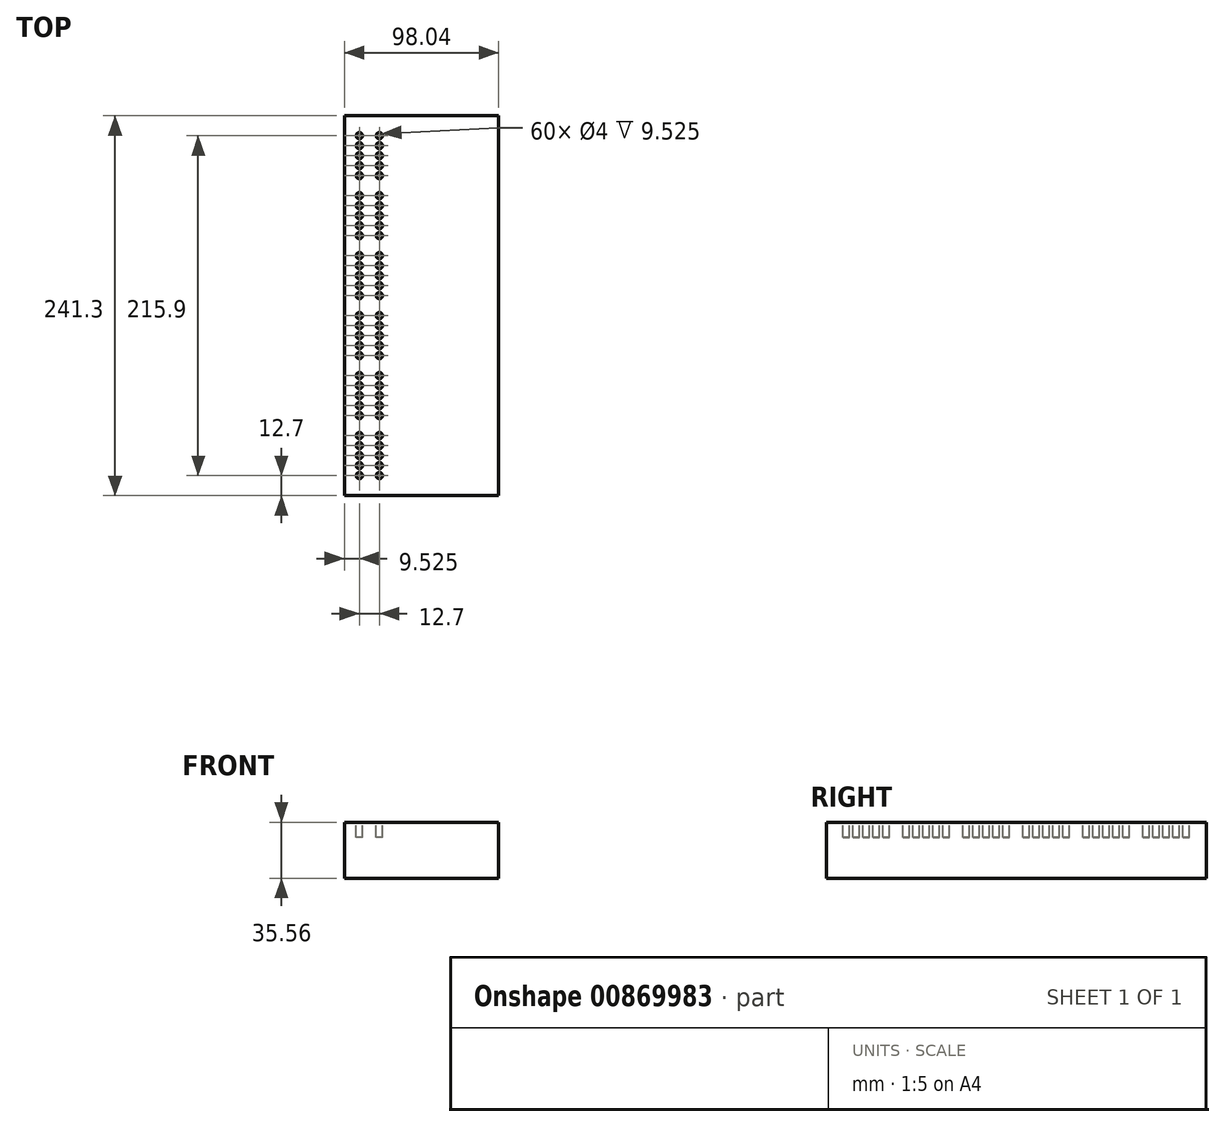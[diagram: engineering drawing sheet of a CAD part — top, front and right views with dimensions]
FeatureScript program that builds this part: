
annotation { "Feature Type Name" : "Feature", "Feature Type Description" : "" }
export const myFeature = defineFeature(function(context is Context, id is Id, definition is map)
    precondition{}
    {
        {
            var Q0;
            Q0=qCreatedBy(makeId("Top.planeOp"),FACE);
            var sketch = newSketch(context, id + "F0", { "sketchPlane" : qUnion([Q0])});
            skLineSegment(sketch, "E0.bottom", {"start": v(0, 241.3) * mm, "end": v(98.04, 241.3) * mm});
            skLineSegment(sketch, "E0.top", {"start": v(0, 0) * mm, "end": v(98.04, 0) * mm});
            skLineSegment(sketch, "E0.left", {"start": v(0, 241.3) * mm, "end": v(0, 0) * mm});
            skLineSegment(sketch, "E0.right", {"start": v(98.04, 241.3) * mm, "end": v(98.04, 0) * mm});
            skSolve(sketch);
        }
        {
            var Q0;
            Q0=makeQuery(id+"F0.imprint","IMPRINT",FACE,{"disambiguationData":[TD([[makeQuery(id+"F0.imprint","IMPRINT",EDGE,{"derivedFrom":sQuery(id+"F0.wireOp",EDGE,"E0.bottom")}),-1.0]])]});
            extrude(context, id + "F1", {"entities" : qUnion([Q0]), "depth" : 35.56 * mm, "offsetDistance" : 25.4 * mm});
        }
        {
            var Q0;
            Q0=makeQuery(id+"F1.opExtrude","CAP_FACE",FACE,{"disambiguationData":[OSD([sQuery(id+"F0.wireOp",EDGE,"E0.bottom"),sQuery(id+"F0.wireOp",EDGE,"E0.top"),sQuery(id+"F0.wireOp",EDGE,"E0.left"),sQuery(id+"F0.wireOp",EDGE,"E0.right")])],"isStart":false});
            var sketch = newSketch(context, id + "F2", { "sketchPlane" : qUnion([Q0])});
            skLineSegment(sketch, "E1", {"start": v(88.52, 241.3) * mm, "end": v(88.52, 0) * mm, "construction": true});
            skLineSegment(sketch, "E2", {"start": v(75.82, 241.3) * mm, "end": v(75.82, 0) * mm, "construction": true});
            skLineSegment(sketch, "E3", {"start": v(22.23, 241.3) * mm, "end": v(22.23, 0) * mm, "construction": true});
            skLineSegment(sketch, "E4", {"start": v(9.53, 241.3) * mm, "end": v(9.53, 0) * mm, "construction": true});
            skLineSegment(sketch, "E5", {"start": v(49.02, 241.3) * mm, "end": v(49.02, 0) * mm, "construction": true});
            skCircle(sketch, "E6", {"center": v(9.53, 12.7) * mm, "radius": 2 * mm});
            skCircle(sketch, "E7", {"center": v(9.53, 19.05) * mm, "radius": 2 * mm});
            skCircle(sketch, "E8", {"center": v(9.53, 25.4) * mm, "radius": 2 * mm});
            skCircle(sketch, "E9", {"center": v(9.53, 31.75) * mm, "radius": 2 * mm});
            skCircle(sketch, "E10", {"center": v(9.53, 38.1) * mm, "radius": 2 * mm});
            skCircle(sketch, "E11.1.0.0", {"center": v(22.23, 38.1) * mm, "radius": 2 * mm});
            skCircle(sketch, "E11.1.0.1", {"center": v(22.23, 31.75) * mm, "radius": 2 * mm});
            skCircle(sketch, "E11.1.0.2", {"center": v(22.23, 25.4) * mm, "radius": 2 * mm});
            skCircle(sketch, "E11.1.0.3", {"center": v(22.23, 19.05) * mm, "radius": 2 * mm});
            skCircle(sketch, "E11.1.0.4", {"center": v(22.23, 12.7) * mm, "radius": 2 * mm});
            skLineSegment(sketch, "E11.direction1", {"start": v(9.53, 12.7) * mm, "end": v(22.23, 12.7) * mm, "construction": true});
            skCircle(sketch, "E12.0.1.0", {"center": v(9.53, 76.2) * mm, "radius": 2 * mm});
            skCircle(sketch, "E12.0.1.1", {"center": v(9.53, 69.85) * mm, "radius": 2 * mm});
            skCircle(sketch, "E12.0.1.2", {"center": v(9.53, 63.5) * mm, "radius": 2 * mm});
            skCircle(sketch, "E12.0.1.3", {"center": v(9.53, 57.15) * mm, "radius": 2 * mm});
            skCircle(sketch, "E12.0.1.4", {"center": v(9.53, 50.8) * mm, "radius": 2 * mm});
            skCircle(sketch, "E12.0.1.5", {"center": v(22.23, 50.8) * mm, "radius": 2 * mm});
            skCircle(sketch, "E12.0.1.6", {"center": v(22.23, 57.15) * mm, "radius": 2 * mm});
            skCircle(sketch, "E12.0.1.7", {"center": v(22.23, 63.5) * mm, "radius": 2 * mm});
            skCircle(sketch, "E12.0.1.8", {"center": v(22.23, 76.2) * mm, "radius": 2 * mm});
            skCircle(sketch, "E12.0.1.9", {"center": v(22.23, 69.85) * mm, "radius": 2 * mm});
            skLineSegment(sketch, "E12.direction1", {"start": v(9.53, 12.7) * mm, "end": v(34.93, 12.7) * mm, "construction": true});
            skLineSegment(sketch, "E12.direction2", {"start": v(9.53, 12.7) * mm, "end": v(9.53, 50.8) * mm, "construction": true});
            skCircle(sketch, "E13.0.0.2", {"center": v(9.53, 114.3) * mm, "radius": 2 * mm});
            skCircle(sketch, "E13.2.0.2", {"center": v(9.53, 107.95) * mm, "radius": 2 * mm});
            skCircle(sketch, "E13.4.0.2", {"center": v(9.53, 101.6) * mm, "radius": 2 * mm});
            skCircle(sketch, "E13.6.0.2", {"center": v(9.53, 95.25) * mm, "radius": 2 * mm});
            skCircle(sketch, "E13.8.0.2", {"center": v(9.53, 88.9) * mm, "radius": 2 * mm});
            skCircle(sketch, "E13.10.0.2", {"center": v(22.23, 88.9) * mm, "radius": 2 * mm});
            skCircle(sketch, "E13.12.0.2", {"center": v(22.23, 95.25) * mm, "radius": 2 * mm});
            skCircle(sketch, "E13.14.0.2", {"center": v(22.23, 101.6) * mm, "radius": 2 * mm});
            skCircle(sketch, "E13.16.0.2", {"center": v(22.23, 114.3) * mm, "radius": 2 * mm});
            skCircle(sketch, "E13.18.0.2", {"center": v(22.23, 107.95) * mm, "radius": 2 * mm});
            skCircle(sketch, "E13.0.0.3", {"center": v(9.53, 152.4) * mm, "radius": 2 * mm});
            skCircle(sketch, "E13.2.0.3", {"center": v(9.53, 146.05) * mm, "radius": 2 * mm});
            skCircle(sketch, "E13.4.0.3", {"center": v(9.53, 139.7) * mm, "radius": 2 * mm});
            skCircle(sketch, "E13.6.0.3", {"center": v(9.53, 133.35) * mm, "radius": 2 * mm});
            skCircle(sketch, "E13.8.0.3", {"center": v(9.53, 127) * mm, "radius": 2 * mm});
            skCircle(sketch, "E13.10.0.3", {"center": v(22.23, 127) * mm, "radius": 2 * mm});
            skCircle(sketch, "E13.12.0.3", {"center": v(22.23, 133.35) * mm, "radius": 2 * mm});
            skCircle(sketch, "E13.14.0.3", {"center": v(22.23, 139.7) * mm, "radius": 2 * mm});
            skCircle(sketch, "E13.16.0.3", {"center": v(22.23, 152.4) * mm, "radius": 2 * mm});
            skCircle(sketch, "E13.18.0.3", {"center": v(22.23, 146.05) * mm, "radius": 2 * mm});
            skCircle(sketch, "E13.0.0.4", {"center": v(9.53, 190.5) * mm, "radius": 2 * mm});
            skCircle(sketch, "E13.2.0.4", {"center": v(9.53, 184.15) * mm, "radius": 2 * mm});
            skCircle(sketch, "E13.4.0.4", {"center": v(9.53, 177.8) * mm, "radius": 2 * mm});
            skCircle(sketch, "E13.6.0.4", {"center": v(9.53, 171.45) * mm, "radius": 2 * mm});
            skCircle(sketch, "E13.8.0.4", {"center": v(9.53, 165.1) * mm, "radius": 2 * mm});
            skCircle(sketch, "E13.10.0.4", {"center": v(22.23, 165.1) * mm, "radius": 2 * mm});
            skCircle(sketch, "E13.12.0.4", {"center": v(22.23, 171.45) * mm, "radius": 2 * mm});
            skCircle(sketch, "E13.14.0.4", {"center": v(22.23, 177.8) * mm, "radius": 2 * mm});
            skCircle(sketch, "E13.16.0.4", {"center": v(22.23, 190.5) * mm, "radius": 2 * mm});
            skCircle(sketch, "E13.18.0.4", {"center": v(22.23, 184.15) * mm, "radius": 2 * mm});
            skCircle(sketch, "E13.0.0.5", {"center": v(9.53, 228.6) * mm, "radius": 2 * mm});
            skCircle(sketch, "E13.2.0.5", {"center": v(9.53, 222.25) * mm, "radius": 2 * mm});
            skCircle(sketch, "E13.4.0.5", {"center": v(9.53, 215.9) * mm, "radius": 2 * mm});
            skCircle(sketch, "E13.6.0.5", {"center": v(9.53, 209.55) * mm, "radius": 2 * mm});
            skCircle(sketch, "E13.8.0.5", {"center": v(9.53, 203.2) * mm, "radius": 2 * mm});
            skCircle(sketch, "E13.10.0.5", {"center": v(22.23, 203.2) * mm, "radius": 2 * mm});
            skCircle(sketch, "E13.12.0.5", {"center": v(22.23, 209.55) * mm, "radius": 2 * mm});
            skCircle(sketch, "E13.14.0.5", {"center": v(22.23, 215.9) * mm, "radius": 2 * mm});
            skCircle(sketch, "E13.16.0.5", {"center": v(22.23, 228.6) * mm, "radius": 2 * mm});
            skCircle(sketch, "E13.18.0.5", {"center": v(22.23, 222.25) * mm, "radius": 2 * mm});
            skSolve(sketch);
        }
        {
            var Q0;
            Q0 = qSketchRegion(id + "F2", true);
            extrude(context, id + "F3", {"entities" : qUnion([Q0]), "operationType" : NewBodyOperationType.REMOVE, "oppositeDirection" : true, "depth" : 9.52 * mm, "offsetDistance" : 25.4 * mm});
        }
    });
